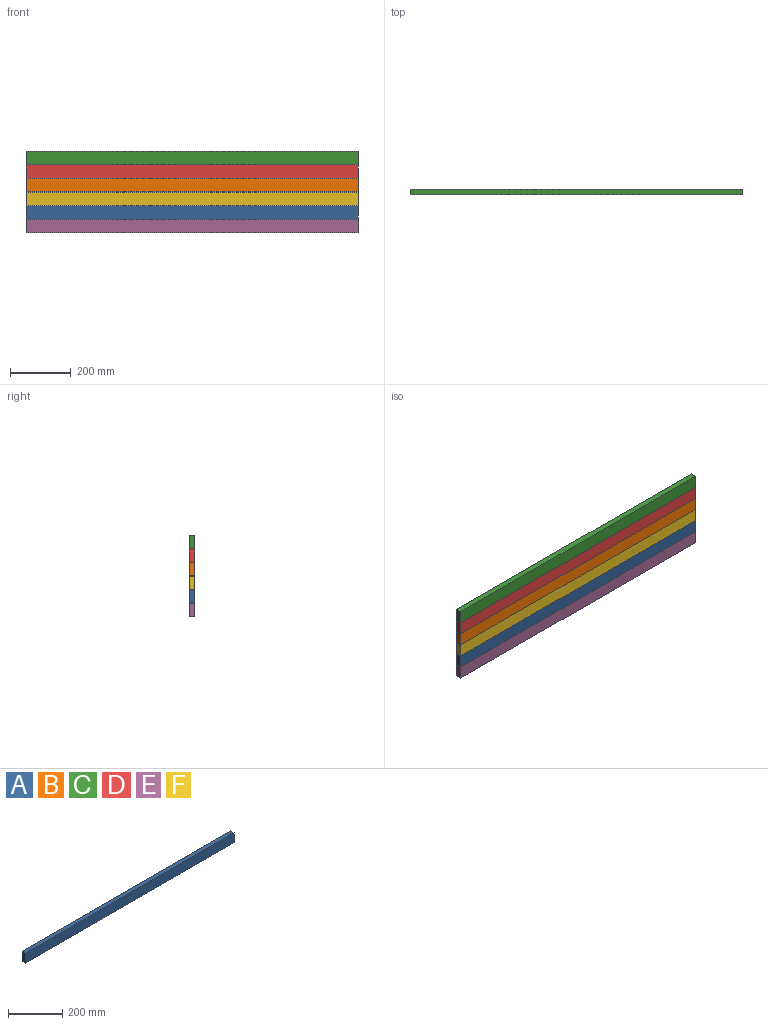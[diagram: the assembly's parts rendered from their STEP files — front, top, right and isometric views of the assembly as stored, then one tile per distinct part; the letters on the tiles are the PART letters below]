
ASSEMBLY  parts=6 mates=1
PART A: 6 faces, bbox 1089x19.1x44.5 mm
  f0: plane 44.45x19.05mm, normal (-1,0,0), area 846.8mm2, adj f1,f3,f4,f5
  f1: plane 1089.03x19.05mm, normal (0,0,-1), area 20745.9mm2, adj f0,f2,f4,f5
  f2: plane 44.45x19.05mm, normal (1,0,0), area 846.8mm2, adj f1,f3,f4,f5
  f3: plane 1089.03x19.05mm, normal (0,0,1), area 20745.9mm2, adj f0,f2,f4,f5
  f4: plane 1089.03x44.45mm, normal (0,-1,0), area 48407.2mm2, adj f0,f1,f2,f3
  f5: plane 1089.03x44.45mm, normal (0,1,0), area 48407.2mm2, adj f0,f1,f2,f3
PART B: same geometry as A
PART C: same geometry as A
PART D: same geometry as A
PART E: same geometry as A
PART F: same geometry as A
PLACE A t=(0,19.05,44.45)mm
PLACE B t=(0,19.05,133.35)mm
PLACE C t=(0,19.05,222.25)mm
PLACE D t=(0,19.05,177.8)mm
PLACE E t=(0,19.05,0)mm
PLACE F t=(0,19.05,88.9)mm
MATE fastened E.f3 <-> A.f1  axis (0,0,1) through (544.51,9.52,44.45)mm
